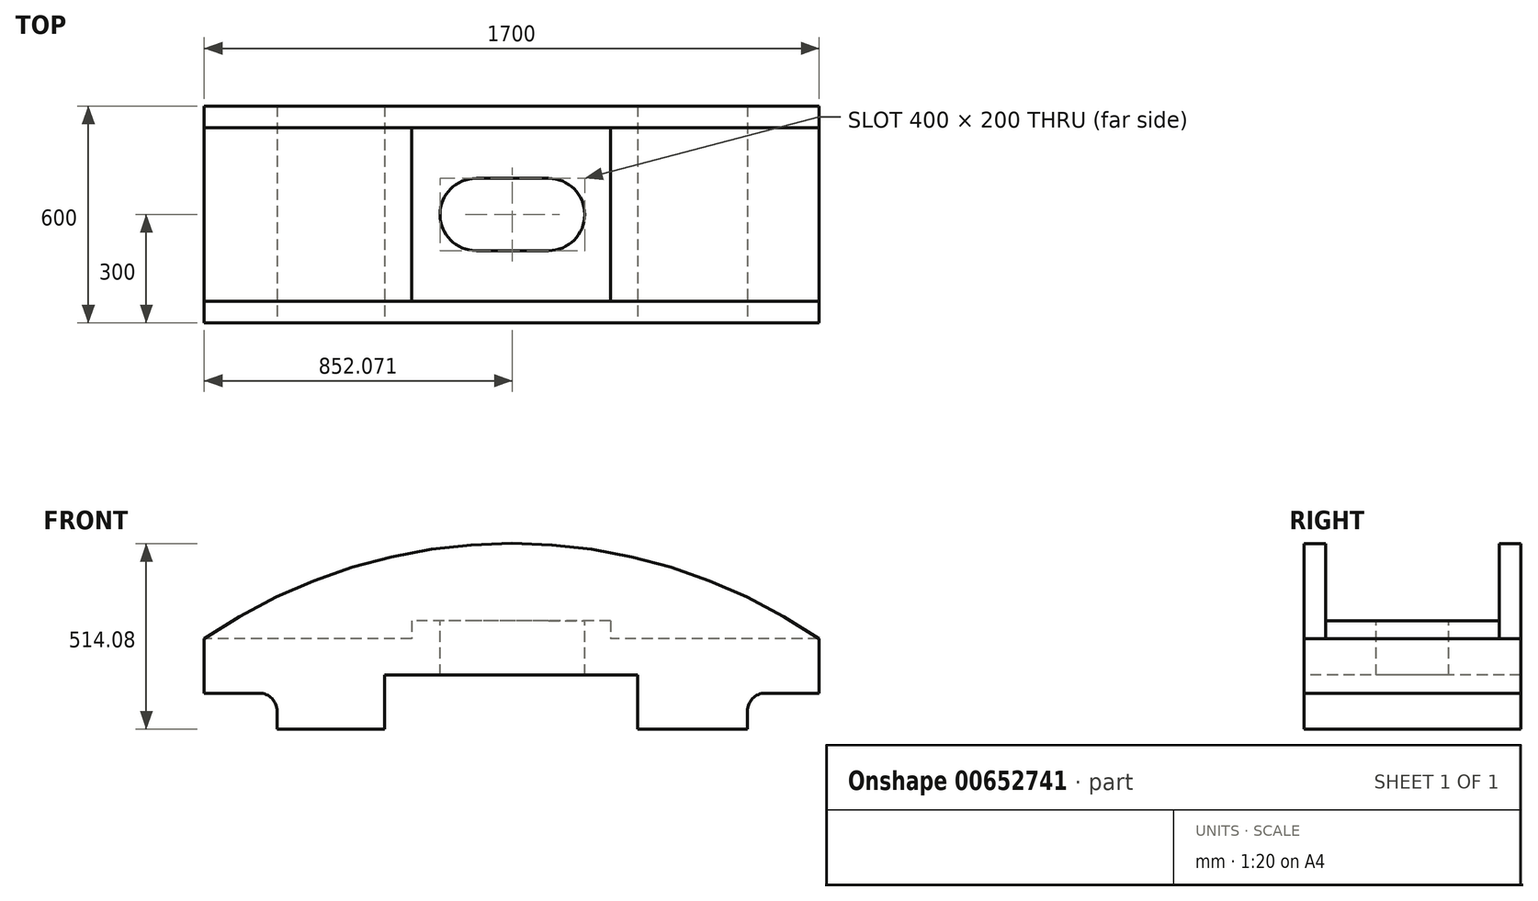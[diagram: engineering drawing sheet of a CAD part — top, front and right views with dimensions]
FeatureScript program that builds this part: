
annotation { "Feature Type Name" : "Feature", "Feature Type Description" : "" }
export const myFeature = defineFeature(function(context is Context, id is Id, definition is map)
    precondition{}
    {
        {
            var Q0;
            Q0=qCreatedBy(makeId("Top.planeOp"),FACE);
            var sketch = newSketch(context, id + "F0", { "sketchPlane" : qUnion([Q0])});
            skLineSegment(sketch, "E0.bottom", {"start": v(-848.22, -240) * mm, "end": v(851.78, -240) * mm});
            skLineSegment(sketch, "E0.top", {"start": v(-848.22, 240) * mm, "end": v(851.78, 240) * mm});
            skLineSegment(sketch, "E0.left", {"start": v(-848.22, -240) * mm, "end": v(-848.22, 240) * mm});
            skLineSegment(sketch, "E0.right", {"start": v(851.78, -240) * mm, "end": v(851.78, 240) * mm});
            skPoint(sketch, "E0.middle", {"position": v(1.78, 0) * mm});
            skSolve(sketch);
        }
        {
            var Q0;
            Q0 = qSketchRegion(id + "F0", true);
            extrude(context, id + "F1", {"entities" : qUnion([Q0]), "depth" : 250 * mm, "offsetDistance" : 25 * mm});
        }
        {
            var Q0;
            Q0=makeQuery(id+"F1.opExtrude","CAP_FACE",FACE,{"disambiguationData":[OSD([sQuery(id+"F0.wireOp",EDGE,"E0.bottom"),sQuery(id+"F0.wireOp",EDGE,"E0.top"),sQuery(id+"F0.wireOp",EDGE,"E0.left"),sQuery(id+"F0.wireOp",EDGE,"E0.right")])],"isStart":false});
            var sketch = newSketch(context, id + "F2", { "sketchPlane" : qUnion([Q0])});
            skLineSegment(sketch, "E1.bottom", {"start": v(851.78, -240) * mm, "end": v(-848.22, -240) * mm});
            skLineSegment(sketch, "E1.top", {"start": v(851.78, -300) * mm, "end": v(-848.22, -300) * mm});
            skLineSegment(sketch, "E1.left", {"start": v(851.78, -240) * mm, "end": v(851.78, -300) * mm});
            skLineSegment(sketch, "E1.right", {"start": v(-848.22, -240) * mm, "end": v(-848.22, -300) * mm});
            skLineSegment(sketch, "E2.bottom", {"start": v(851.78, 240) * mm, "end": v(-848.22, 240) * mm});
            skLineSegment(sketch, "E2.top", {"start": v(851.78, 300) * mm, "end": v(-848.22, 300) * mm});
            skLineSegment(sketch, "E2.left", {"start": v(851.78, 240) * mm, "end": v(851.78, 300) * mm});
            skLineSegment(sketch, "E2.right", {"start": v(-848.22, 240) * mm, "end": v(-848.22, 300) * mm});
            skSolve(sketch);
        }
        {
            var Q0;
            Q0 = qSketchRegion(id + "F2", true);
            extrude(context, id + "F3", {"entities" : qUnion([Q0]), "operationType" : NewBodyOperationType.ADD, "oppositeDirection" : true, "depth" : 250 * mm, "offsetDistance" : 25 * mm});
        }
        {
            var Q0;
            Q0=makeQuery(id+"F3.opExtrude","SWEPT_FACE",FACE,{"disambiguationData":[OSD([sQuery(id+"F2.wireOp",EDGE,"E1.top")])]});
            var sketch = newSketch(context, id + "F4", { "sketchPlane" : qUnion([Q0])});
            skArc(sketch, "E3", {"start": v(851.78, 250) * mm, "mid": v(1.78, 514.08) * mm, "end": v(-848.22, 250) * mm});
            skSolve(sketch);
        }
        {
            var Q0;
            Q0 = qSketchRegion(id + "F4", true);
            var Q1;
            Q1=makeQuery(id+"F4.imprint","IMPRINT",FACE,{"disambiguationData":[TD([[makeQuery(id+"F4.imprint","IMPRINT",EDGE,{"derivedFrom":sQuery(id+"F4.wireOp",EDGE,"E3")}),1.0]])]});
            extrude(context, id + "F5", {"entities" : qUnion([Q0, Q1]), "operationType" : NewBodyOperationType.ADD, "oppositeDirection" : true, "depth" : 60 * mm, "offsetDistance" : 25 * mm});
        }
        {
            var Q0;
            Q0=makeQuery(id+"F3.opExtrude","SWEPT_FACE",FACE,{"disambiguationData":[OSD([sQuery(id+"F2.wireOp",EDGE,"E2.top")])]});
            var sketch = newSketch(context, id + "F6", { "sketchPlane" : qUnion([Q0])});
            skArc(sketch, "E4", {"start": v(848.22, 250) * mm, "mid": v(-1.78, 514.08) * mm, "end": v(-851.78, 250) * mm});
            skSolve(sketch);
        }
        {
            var Q0;
            Q0 = qSketchRegion(id + "F6", true);
            var Q1;
            Q1=makeQuery(id+"F6.imprint","IMPRINT",FACE,{"disambiguationData":[TD([[makeQuery(id+"F6.imprint","IMPRINT",EDGE,{"derivedFrom":sQuery(id+"F6.wireOp",EDGE,"E4")}),1.0]])]});
            extrude(context, id + "F7", {"entities" : qUnion([Q0, Q1]), "operationType" : NewBodyOperationType.ADD, "oppositeDirection" : true, "depth" : 60 * mm, "offsetDistance" : 25 * mm});
        }
        {
            var Q0;
            Q0=makeQuery(id+"F3.boolean.opBoolean","MERGE",FACE,{"derivedFrom":[makeQuery(id+"F1.opExtrude","CAP_FACE",FACE,{"disambiguationData":[OSD([sQuery(id+"F0.wireOp",EDGE,"E0.bottom"),sQuery(id+"F0.wireOp",EDGE,"E0.top"),sQuery(id+"F0.wireOp",EDGE,"E0.left"),sQuery(id+"F0.wireOp",EDGE,"E0.right")])],"isStart":false}),makeQuery(id+"F3.opExtrude","CAP_FACE",FACE,{"disambiguationData":[OSD([sQuery(id+"F2.wireOp",EDGE,"E1.bottom"),sQuery(id+"F2.wireOp",EDGE,"E1.top"),sQuery(id+"F2.wireOp",EDGE,"E1.left"),sQuery(id+"F2.wireOp",EDGE,"E1.right")])],"isStart":true}),makeQuery(id+"F3.opExtrude","CAP_FACE",FACE,{"disambiguationData":[OSD([sQuery(id+"F2.wireOp",EDGE,"E2.bottom"),sQuery(id+"F2.wireOp",EDGE,"E2.top"),sQuery(id+"F2.wireOp",EDGE,"E2.left"),sQuery(id+"F2.wireOp",EDGE,"E2.right")])],"isStart":true})]});
            var sketch = newSketch(context, id + "F8", { "sketchPlane" : qUnion([Q0])});
            skLineSegment(sketch, "E5.bottom", {"start": v(-275, -240) * mm, "end": v(275, -240) * mm});
            skLineSegment(sketch, "E5.top", {"start": v(-275, 240) * mm, "end": v(275, 240) * mm});
            skLineSegment(sketch, "E5.left", {"start": v(-275, -240) * mm, "end": v(-275, 240) * mm});
            skLineSegment(sketch, "E5.right", {"start": v(275, -240) * mm, "end": v(275, 240) * mm});
            skPoint(sketch, "E5.middle", {"position": v(0, 0) * mm});
            skSolve(sketch);
        }
        {
            var Q0;
            Q0 = qSketchRegion(id + "F8", true);
            extrude(context, id + "F9", {"entities" : qUnion([Q0]), "operationType" : NewBodyOperationType.ADD, "depth" : 50 * mm, "offsetDistance" : 25 * mm});
        }
        {
            var Q0;
            Q0=makeQuery(id+"F9.opExtrude","CAP_FACE",FACE,{"disambiguationData":[OSD([sQuery(id+"F8.wireOp",EDGE,"E5.bottom"),sQuery(id+"F8.wireOp",EDGE,"E5.top"),sQuery(id+"F8.wireOp",EDGE,"E5.left"),sQuery(id+"F8.wireOp",EDGE,"E5.right")])],"isStart":false});
            var sketch = newSketch(context, id + "F10", { "sketchPlane" : qUnion([Q0])});
            skArc(sketch, "E6", {"start": v(103.85, -100) * mm, "mid": v(203.85, 0) * mm, "end": v(103.85, 100) * mm});
            skArc(sketch, "E7", {"start": v(-96.15, 100) * mm, "mid": v(-196.15, 0) * mm, "end": v(-96.15, -100) * mm});
            skLineSegment(sketch, "E8", {"start": v(103.85, -100) * mm, "end": v(-96.15, -100) * mm});
            skLineSegment(sketch, "E9", {"start": v(-96.15, 100) * mm, "end": v(103.85, 100) * mm});
            skSolve(sketch);
        }
        {
            var Q0;
            Q0 = qSketchRegion(id + "F10", true);
            extrude(context, id + "F11", {"entities" : qUnion([Q0]), "operationType" : NewBodyOperationType.REMOVE, "endBound" : BoundingType.THROUGH_ALL, "oppositeDirection" : true, "depth" : 25 * mm, "offsetDistance" : 25 * mm});
        }
        {
            var Q0;
            {var subQ0=sQuery(id+"F2.wireOp",EDGE,"E1.top");Q0=makeQuery(id+"F5.boolean.opBoolean","MERGE",FACE,{"derivedFrom":[makeQuery(id+"F3.opExtrude","SWEPT_FACE",FACE,{"disambiguationData":[OSD([subQ0])]}),makeQuery(id+"F5.opExtrude","CAP_FACE",FACE,{"disambiguationData":[OSD([subQ0,sQuery(id+"F4.wireOp",EDGE,"E3")])],"isStart":true})]});}
            var sketch = newSketch(context, id + "F12", { "sketchPlane" : qUnion([Q0])});
            skLineSegment(sketch, "E10.bottom", {"start": v(-350, 150) * mm, "end": v(350, 150) * mm});
            skLineSegment(sketch, "E10.top", {"start": v(-350, -150) * mm, "end": v(350, -150) * mm});
            skLineSegment(sketch, "E10.left", {"start": v(-350, 150) * mm, "end": v(-350, -150) * mm});
            skLineSegment(sketch, "E10.right", {"start": v(350, 150) * mm, "end": v(350, -150) * mm});
            skPoint(sketch, "E10.middle", {"position": v(0, 0) * mm});
            skSolve(sketch);
        }
        {
            var Q0;
            Q0 = qSketchRegion(id + "F12", true);
            extrude(context, id + "F13", {"entities" : qUnion([Q0]), "operationType" : NewBodyOperationType.REMOVE, "endBound" : BoundingType.THROUGH_ALL, "oppositeDirection" : true, "depth" : 25 * mm, "offsetDistance" : 25 * mm});
        }
        {
            var Q0;
            {var subQ0=sQuery(id+"F2.wireOp",EDGE,"E1.top");Q0=makeQuery(id+"F5.boolean.opBoolean","MERGE",FACE,{"derivedFrom":[makeQuery(id+"F3.opExtrude","SWEPT_FACE",FACE,{"disambiguationData":[OSD([subQ0])]}),makeQuery(id+"F5.opExtrude","CAP_FACE",FACE,{"disambiguationData":[OSD([subQ0,sQuery(id+"F4.wireOp",EDGE,"E3")])],"isStart":true})]});}
            var sketch = newSketch(context, id + "F14", { "sketchPlane" : qUnion([Q0])});
            skLineSegment(sketch, "E11.bottom", {"start": v(-646.44, 100) * mm, "end": v(-1050, 100) * mm});
            skLineSegment(sketch, "E11.top", {"start": v(-646.44, -100) * mm, "end": v(-1050, -100) * mm});
            skLineSegment(sketch, "E11.left", {"start": v(-1050, 100) * mm, "end": v(-1050, -100) * mm});
            skLineSegment(sketch, "E11.right", {"start": v(-646.44, 100) * mm, "end": v(-646.44, -100) * mm});
            skPoint(sketch, "E11.middle", {"position": v(-848.22, 0) * mm});
            skSolve(sketch);
        }
        {
            var Q0;
            Q0 = qSketchRegion(id + "F14", true);
            extrude(context, id + "F15", {"entities" : qUnion([Q0]), "operationType" : NewBodyOperationType.REMOVE, "endBound" : BoundingType.THROUGH_ALL, "oppositeDirection" : true, "depth" : 25 * mm, "offsetDistance" : 25 * mm});
        }
        {
            var Q0;
            Q0=makeQuery(id+"F15.boolean.opBoolean","COPY",EDGE,{"derivedFrom":makeQuery(id+"F15.opExtrude","SWEPT_EDGE",EDGE,{"disambiguationData":[OSD([sQuery(id+"F14.wireOp",EDGE,"E11.bottom"),sQuery(id+"F14.wireOp",EDGE,"E11.right")])]})});
            fillet(context, id + "F16", {"entities" : qUnion([Q0]), "radius" : 50 * mm, "tangentPropagation" : true, "allowEdgeOverflow" : false});
        }
        {
            var Q0;
            {var subQ0=sQuery(id+"F2.wireOp",EDGE,"E1.top");Q0=makeQuery(id+"F5.boolean.opBoolean","MERGE",FACE,{"derivedFrom":[makeQuery(id+"F3.opExtrude","SWEPT_FACE",FACE,{"disambiguationData":[OSD([subQ0])]}),makeQuery(id+"F5.opExtrude","CAP_FACE",FACE,{"disambiguationData":[OSD([subQ0,sQuery(id+"F4.wireOp",EDGE,"E3")])],"isStart":true})]});}
            var sketch = newSketch(context, id + "F17", { "sketchPlane" : qUnion([Q0])});
            skLineSegment(sketch, "E12.bottom", {"start": v(653.56, 100) * mm, "end": v(1050, 100) * mm});
            skLineSegment(sketch, "E12.top", {"start": v(653.56, -100) * mm, "end": v(1050, -100) * mm});
            skLineSegment(sketch, "E12.left", {"start": v(1050, 100) * mm, "end": v(1050, -100) * mm});
            skLineSegment(sketch, "E12.right", {"start": v(653.56, 100) * mm, "end": v(653.56, -100) * mm});
            skPoint(sketch, "E12.middle", {"position": v(851.78, 0) * mm});
            skSolve(sketch);
        }
        {
            var Q0;
            Q0 = qSketchRegion(id + "F17", true);
            extrude(context, id + "F18", {"entities" : qUnion([Q0]), "operationType" : NewBodyOperationType.REMOVE, "endBound" : BoundingType.THROUGH_ALL, "oppositeDirection" : true, "depth" : 25 * mm, "offsetDistance" : 25 * mm});
        }
        {
            var Q0;
            Q0=makeQuery(id+"F18.boolean.opBoolean","COPY",EDGE,{"derivedFrom":makeQuery(id+"F18.opExtrude","SWEPT_EDGE",EDGE,{"disambiguationData":[OSD([sQuery(id+"F17.wireOp",EDGE,"E12.bottom"),sQuery(id+"F17.wireOp",EDGE,"E12.right")])]})});
            fillet(context, id + "F19", {"entities" : qUnion([Q0]), "radius" : 50 * mm, "tangentPropagation" : true, "allowEdgeOverflow" : false});
        }
    });
